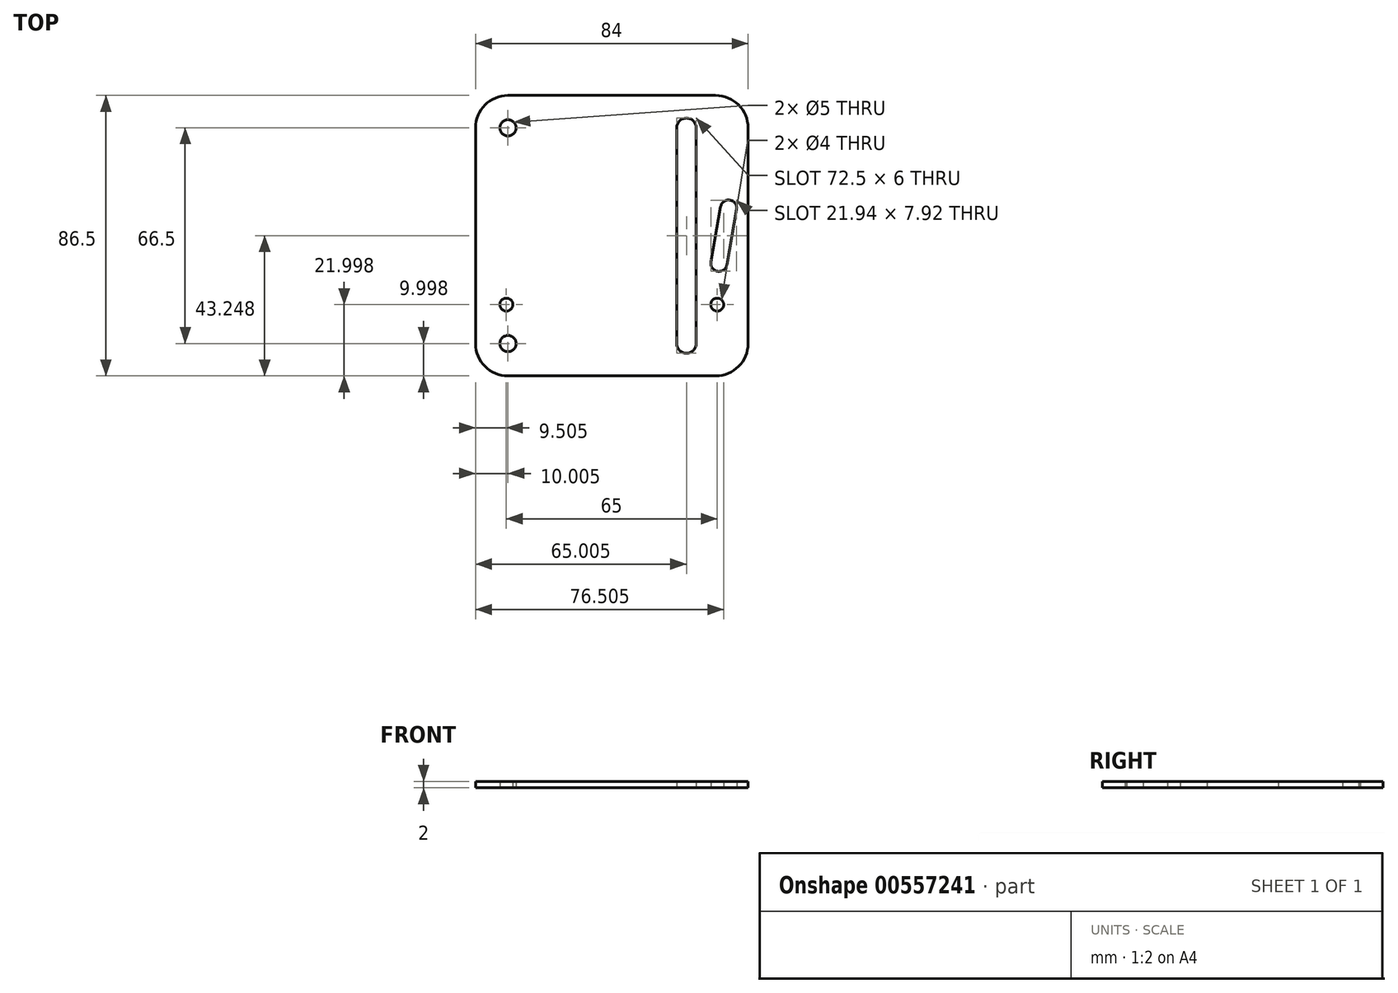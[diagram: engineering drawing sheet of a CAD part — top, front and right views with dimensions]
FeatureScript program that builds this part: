
annotation { "Feature Type Name" : "Feature", "Feature Type Description" : "" }
export const myFeature = defineFeature(function(context is Context, id is Id, definition is map)
    precondition{}
    {
        {
            var Q0;
            Q0=qCreatedBy(makeId("Top.planeOp"),FACE);
            var sketch = newSketch(context, id + "F0", { "sketchPlane" : qUnion([Q0])});
            skLineSegment(sketch, "E0.bottom", {"start": v(-35.6, 56.65) * mm, "end": v(28.4, 56.65) * mm});
            skLineSegment(sketch, "E0.top", {"start": v(-35.6, -29.85) * mm, "end": v(28.4, -29.85) * mm});
            skLineSegment(sketch, "E0.left", {"start": v(-45.6, 46.65) * mm, "end": v(-45.6, -19.85) * mm});
            skLineSegment(sketch, "E0.right", {"start": v(38.4, 46.65) * mm, "end": v(38.4, -19.85) * mm});
            skCircle(sketch, "E1", {"center": v(-35.6, 46.65) * mm, "radius": 2.5 * mm});
            skCircle(sketch, "E2", {"center": v(-35.6, -19.85) * mm, "radius": 2.5 * mm});
            skArc(sketch, "E3.0.startCap", {"start": v(31.86, 4.46) * mm, "mid": v(28.96, 2.43) * mm, "end": v(26.93, 5.33) * mm});
            skArc(sketch, "E3.0.endCap", {"start": v(29.93, 22.34) * mm, "mid": v(32.83, 24.37) * mm, "end": v(34.86, 21.47) * mm});
            skLineSegment(sketch, "E3.0.left", {"start": v(26.93, 5.33) * mm, "end": v(29.93, 22.34) * mm});
            skLineSegment(sketch, "E3.0.right", {"start": v(31.86, 4.46) * mm, "end": v(34.86, 21.47) * mm});
            skArc(sketch, "E4.0.startCap", {"start": v(16.4, 46.65) * mm, "mid": v(19.4, 49.65) * mm, "end": v(22.4, 46.65) * mm});
            skArc(sketch, "E4.0.endCap", {"start": v(22.4, -19.85) * mm, "mid": v(19.4, -22.85) * mm, "end": v(16.4, -19.85) * mm});
            skLineSegment(sketch, "E4.0.left", {"start": v(22.4, 46.65) * mm, "end": v(22.4, -19.85) * mm});
            skLineSegment(sketch, "E4.0.right", {"start": v(16.4, 46.65) * mm, "end": v(16.4, -19.85) * mm});
            skPoint(sketch, "E5.visualSharp", {"position": v(-45.6, 56.65) * mm});
            skArc(sketch, "E5.filletArc", {"start": v(-35.6, 56.65) * mm, "mid": v(-42.68, 53.72) * mm, "end": v(-45.6, 46.65) * mm});
            skPoint(sketch, "E6.visualSharp", {"position": v(38.4, 56.65) * mm});
            skArc(sketch, "E6.filletArc", {"start": v(38.4, 46.65) * mm, "mid": v(35.47, 53.72) * mm, "end": v(28.4, 56.65) * mm});
            skPoint(sketch, "E7.visualSharp", {"position": v(38.4, -29.85) * mm});
            skArc(sketch, "E7.filletArc", {"start": v(28.4, -29.85) * mm, "mid": v(35.47, -26.92) * mm, "end": v(38.4, -19.85) * mm});
            skPoint(sketch, "E8.visualSharp", {"position": v(-45.6, -29.85) * mm});
            skArc(sketch, "E8.filletArc", {"start": v(-45.6, -19.85) * mm, "mid": v(-42.68, -26.92) * mm, "end": v(-35.6, -29.85) * mm});
            skCircle(sketch, "E9", {"center": v(-36.1, -7.85) * mm, "radius": 2 * mm});
            skCircle(sketch, "E10", {"center": v(28.9, -7.85) * mm, "radius": 2 * mm});
            skSolve(sketch);
        }
        {
            var Q0;
            Q0 = qSketchRegion(id + "F0", true);
            extrude(context, id + "F1", {"entities" : qUnion([Q0]), "depth" : 2 * mm, "offsetDistance" : 25 * mm});
        }
    });
